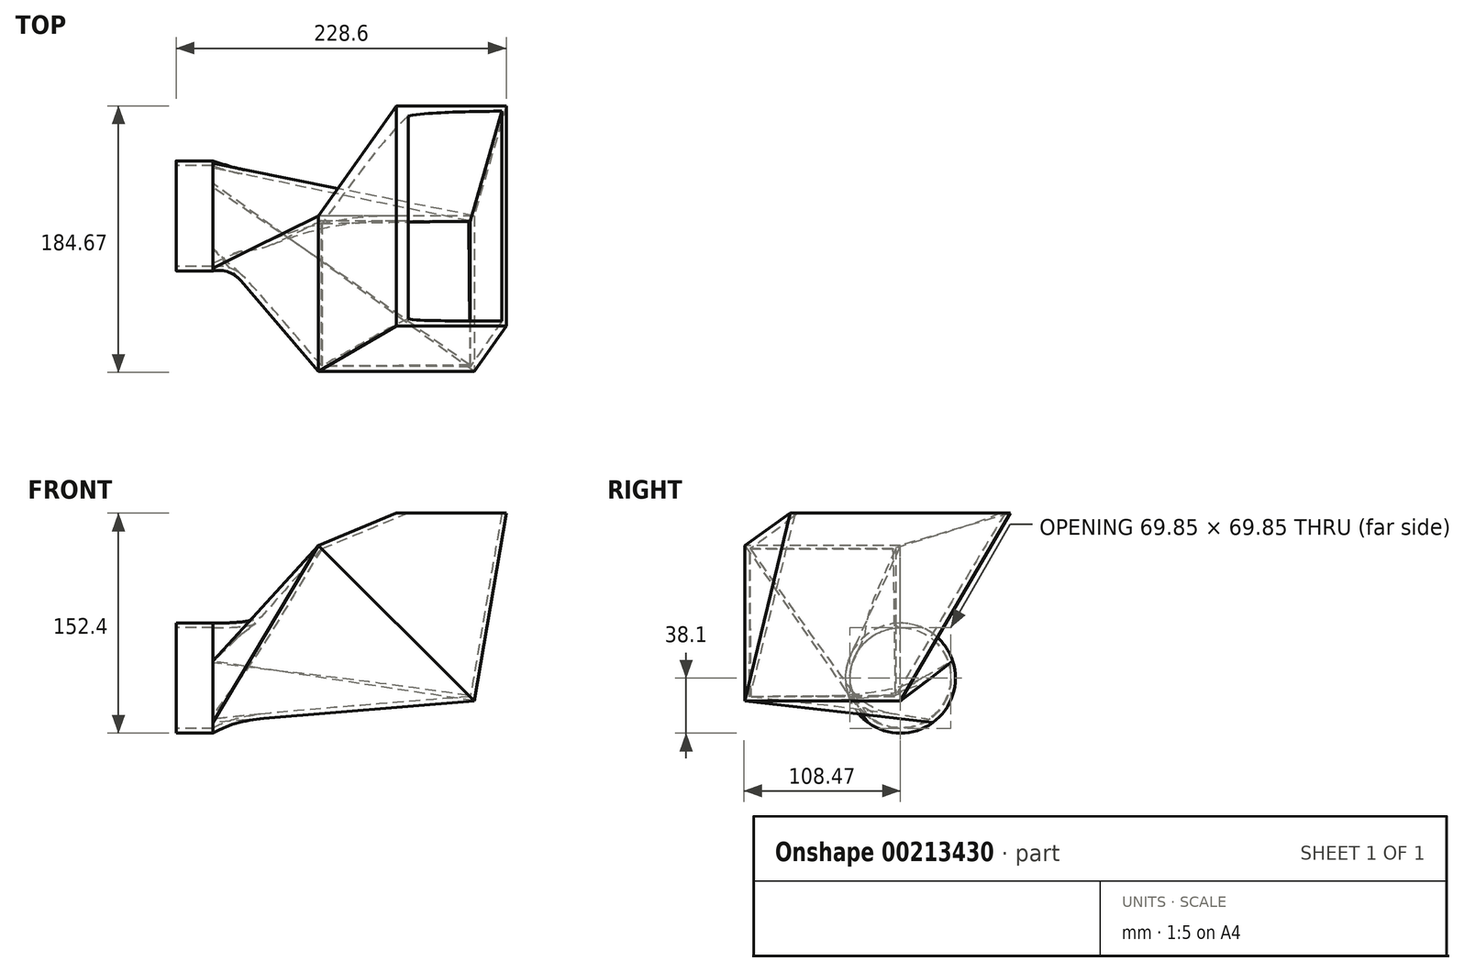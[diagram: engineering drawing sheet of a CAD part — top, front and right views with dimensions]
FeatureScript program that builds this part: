
annotation { "Feature Type Name" : "Feature", "Feature Type Description" : "" }
export const myFeature = defineFeature(function(context is Context, id is Id, definition is map)
    precondition{}
    {
        {
            var Q0;
            Q0=qCreatedBy(makeId("Front.planeOp"),FACE);
            var sketch = newSketch(context, id + "F0", { "sketchPlane" : qUnion([Q0])});
            skLineSegment(sketch, "E0", {"start": v(0, 76.2) * mm, "end": v(0, 0) * mm});
            skLineSegment(sketch, "E1", {"start": v(0, 0) * mm, "end": v(-127, 0) * mm});
            skLineSegment(sketch, "E2", {"start": v(-127, 0) * mm, "end": v(-152.4, 0) * mm});
            skLineSegment(sketch, "E3", {"start": v(76.2, 76.2) * mm, "end": v(0, 0) * mm});
            skSolve(sketch);
        }
        {
            var Q0;
            Q0=sQuery(id+"F0.wireOp",VERTEX,"E0.start");
            var Q1;
            Q1=sQuery(id+"F0.wireOp",EDGE,"E0");
            cPlane(context, id + "F1", {"entities" : qUnion([Q0, Q1]), "cplaneType" : CPlaneType.LINE_POINT, "offset" : 25.4 * mm, "width" : 152.4 * mm, "height" : 152.4 * mm});
        }
        {
            var Q0;
            Q0=sQuery(id+"F0.wireOp",EDGE,"E3");
            var Q1;
            Q1=sQuery(id+"F0.wireOp",VERTEX,"E1.start");
            cPlane(context, id + "F2", {"entities" : qUnion([Q0, Q1]), "cplaneType" : CPlaneType.LINE_POINT, "offset" : 25.4 * mm, "width" : 152.4 * mm, "height" : 152.4 * mm});
        }
        {
            var Q0;
            Q0=sQuery(id+"F0.wireOp",VERTEX,"E2.start");
            var Q1;
            Q1=qCreatedBy(makeId("Right.planeOp"),FACE);
            cPlane(context, id + "F3", {"entities" : qUnion([Q0, Q1]), "cplaneType" : CPlaneType.PLANE_POINT, "offset" : 25.4 * mm, "width" : 152.4 * mm, "height" : 152.4 * mm});
        }
        {
            var Q0;
            Q0=sQuery(id+"F0.wireOp",VERTEX,"E2.end");
            var Q1;
            Q1=qCreatedBy(id+"F3.planeOp",FACE);
            cPlane(context, id + "F4", {"entities" : qUnion([Q0, Q1]), "cplaneType" : CPlaneType.PLANE_POINT, "offset" : 25.4 * mm, "width" : 152.4 * mm, "height" : 152.4 * mm});
        }
        {
            var Q0;
            Q0=qCreatedBy(id+"F1.planeOp",FACE);
            var sketch = newSketch(context, id + "F5", { "sketchPlane" : qUnion([Q0])});
            skLineSegment(sketch, "E4.bottom", {"start": v(0, -76.2) * mm, "end": v(76.2, -76.2) * mm});
            skLineSegment(sketch, "E4.top", {"start": v(0, 76.2) * mm, "end": v(76.2, 76.2) * mm});
            skLineSegment(sketch, "E4.left", {"start": v(0, -76.2) * mm, "end": v(0, 76.2) * mm});
            skLineSegment(sketch, "E4.right", {"start": v(76.2, -76.2) * mm, "end": v(76.2, 76.2) * mm});
            skSolve(sketch);
        }
        {
            var Q0;
            Q0=qCreatedBy(id+"F2.planeOp",FACE);
            var sketch = newSketch(context, id + "F6", { "sketchPlane" : qUnion([Q0])});
            skLineSegment(sketch, "E5.bottom", {"start": v(0, -76.2) * mm, "end": v(107.76, -76.2) * mm});
            skLineSegment(sketch, "E5.top", {"start": v(0, 76.2) * mm, "end": v(107.76, 76.2) * mm});
            skLineSegment(sketch, "E5.left", {"start": v(0, -76.2) * mm, "end": v(0, 76.2) * mm});
            skLineSegment(sketch, "E5.right", {"start": v(107.76, -76.2) * mm, "end": v(107.76, 76.2) * mm});
            skSolve(sketch);
        }
        {
            var Q0;
            Q0=qCreatedBy(id+"F3.planeOp",FACE);
            var sketch = newSketch(context, id + "F7", { "sketchPlane" : qUnion([Q0])});
            skCircle(sketch, "E6", {"center": v(0, -38.1) * mm, "radius": 38.1 * mm});
            skSolve(sketch);
        }
        {
            var Q0;
            Q0=makeQuery(id+"F5.imprint","IMPRINT",FACE,{"disambiguationData":[TD([[makeQuery(id+"F5.imprint","IMPRINT",EDGE,{"derivedFrom":sQuery(id+"F5.wireOp",EDGE,"E4.bottom")}),1.0]])]});
            var Q1;
            Q1=makeQuery(id+"F6.imprint","IMPRINT",FACE,{"disambiguationData":[TD([[makeQuery(id+"F6.imprint","IMPRINT",EDGE,{"derivedFrom":sQuery(id+"F6.wireOp",EDGE,"E5.bottom")}),1.0]])]});
            loft(context, id + "F8", {"sheetProfilesArray" : [{ "sheetProfileEntities" : qUnion([Q0]) }, { "sheetProfileEntities" : qUnion([Q1]) }]});
        }
        {
            var Q1;
            Q1=makeQuery(id+"F8.opLoft","CAP_FACE",FACE,{"disambiguationData":[OSD([makeQuery(id+"F6.imprint","IMPRINT",FACE,{"disambiguationData":[TD([[makeQuery(id+"F6.imprint","IMPRINT",EDGE,{"derivedFrom":sQuery(id+"F6.wireOp",EDGE,"E5.bottom")}),1.0]])]})])],"isStart":true});
            var Q2;
            Q2=makeQuery(id+"F7.imprint","IMPRINT",FACE,{"disambiguationData":[TD([[makeQuery(id+"F7.imprint","IMPRINT",EDGE,{"derivedFrom":sQuery(id+"F7.wireOp",EDGE,"E6")}),1.0]])]});
            var Q3;
            Q3=sQuery(id+"F0.wireOp",EDGE,"E1");
            loft(context, id + "F9", {"addGuides" : true, "sheetProfilesArray" : [{ "sheetProfileEntities" : qUnion([Q1]) }, { "sheetProfileEntities" : qUnion([Q2]) }], "guidesArray" : [{ "guideEntities" : qUnion([Q3]), "guideDerivativeType" : LoftGuideDerivativeType.DEFAULT, "guideDerivativeMagnitude" : 1 }]});
        }
        {
            var Q0;
            Q0=makeQuery(id+"F9.opLoft","CAP_FACE",FACE,{"disambiguationData":[OSD([makeQuery(id+"F7.imprint","IMPRINT",FACE,{"disambiguationData":[TD([[makeQuery(id+"F7.imprint","IMPRINT",EDGE,{"derivedFrom":sQuery(id+"F7.wireOp",EDGE,"E6")}),1.0]])]})])],"isStart":true});
            var Q1;
            Q1=qCreatedBy(id+"F4.planeOp",FACE);
            extrude(context, id + "F10", {"entities" : qUnion([Q0]), "endBound" : BoundingType.UP_TO_SURFACE, "endBoundEntityFace" : qUnion([Q1]), "depth" : 25.4 * mm});
        }
        {
            var Q0;
            Q0=makeQuery(id+"F8.opLoft","CAP_FACE",FACE,{"disambiguationData":[OSD([makeQuery(id+"F5.imprint","IMPRINT",FACE,{"disambiguationData":[TD([[makeQuery(id+"F5.imprint","IMPRINT",EDGE,{"derivedFrom":sQuery(id+"F5.wireOp",EDGE,"E4.bottom")}),1.0]])]})])],"isStart":true});
            var Q1;
            Q1=makeQuery(id+"F8.opLoft","CAP_FACE",FACE,{"disambiguationData":[OSD([makeQuery(id+"F6.imprint","IMPRINT",FACE,{"disambiguationData":[TD([[makeQuery(id+"F6.imprint","IMPRINT",EDGE,{"derivedFrom":sQuery(id+"F6.wireOp",EDGE,"E5.bottom")}),1.0]])]})])],"isStart":true});
            var Q2;
            Q2=makeQuery(id+"F9.opLoft","CAP_FACE",FACE,{"disambiguationData":[OSD([makeQuery(id+"F6.imprint","IMPRINT",FACE,{"disambiguationData":[TD([[makeQuery(id+"F6.imprint","IMPRINT",EDGE,{"derivedFrom":sQuery(id+"F6.wireOp",EDGE,"E5.bottom")}),1.0]])]})])],"isStart":true});
            var Q3;
            Q3=makeQuery(id+"F9.opLoft","CAP_FACE",FACE,{"disambiguationData":[OSD([makeQuery(id+"F7.imprint","IMPRINT",FACE,{"disambiguationData":[TD([[makeQuery(id+"F7.imprint","IMPRINT",EDGE,{"derivedFrom":sQuery(id+"F7.wireOp",EDGE,"E6")}),1.0]])]})])],"isStart":true});
            var Q4;
            Q4=makeQuery(id+"F10.opExtrude","CAP_FACE",FACE,{"disambiguationData":[OSD([makeQuery(id+"F7.imprint","IMPRINT",FACE,{"disambiguationData":[TD([[makeQuery(id+"F7.imprint","IMPRINT",EDGE,{"derivedFrom":sQuery(id+"F7.wireOp",EDGE,"E6")}),1.0]])]})])],"isStart":false});
            var Q5;
            Q5=makeQuery(id+"F10.opExtrude","CAP_FACE",FACE,{"disambiguationData":[OSD([makeQuery(id+"F7.imprint","IMPRINT",FACE,{"disambiguationData":[TD([[makeQuery(id+"F7.imprint","IMPRINT",EDGE,{"derivedFrom":sQuery(id+"F7.wireOp",EDGE,"E6")}),1.0]])]})])],"isStart":true});
            var Q6;
            Q6=makeQuery(id+"F10.opExtrude","CAP_FACE",FACE,{"disambiguationData":[OSD([dummyQuery(id+"F4.planeOp",FACE)])],"isStart":false});
            shell(context, id + "F11", {"entities" : qUnion([Q0, Q1, Q2, Q3, Q4, Q5, Q6]), "thickness" : 3.17 * mm});
        }
    });
